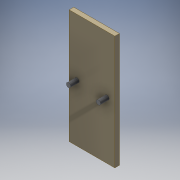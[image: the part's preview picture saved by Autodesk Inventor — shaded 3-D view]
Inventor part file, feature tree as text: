
AUTODESK INVENTOR PART (.ipt)
format: ipt  version: 2018.1 (Build 221151000, 151)  size: 106,496 bytes
history: native  units: in
note: dims shown in document units (in); Inventor stores cm internally (conversion verified against a paired STEP export)
features: extrude x2, thread x2, sketch x2, imported_body x1, other x1
ambient origin geometry x8: Origin, YZ Plane, XZ Plane, XY Plane, X Axis, Y Axis, Z Axis, Center Point
bodies: Body1 (feature_tree), Body2 (feature_tree)
feature tree (8):
  imported_body  "Base"
  extrude  "Extrusion1"  Depth=5.0in
  extrude  "Extrusion2"  Depth=0.375in
  thread  "Thread1"  [1 undecoded]
  thread  "Thread2"  [1 undecoded]
  sketch  "Sketch1"  dims[d0=2.0in d2=5.0in]
  sketch  "Sketch2"  dims[d3=0.2in d4=0.0in d5=0.188in d8=1.31in d9=0.655in d10=0.375in d11=0.0in d12=1.0in d13=0.0in d14=1.0in d15=0.0in]
  other  "Screws"
note: 2 required parameter values undecoded (feature->parameter linkage not recoverable at this tier; creation-order binding heuristic only, values carry confidence <= 0.55)
